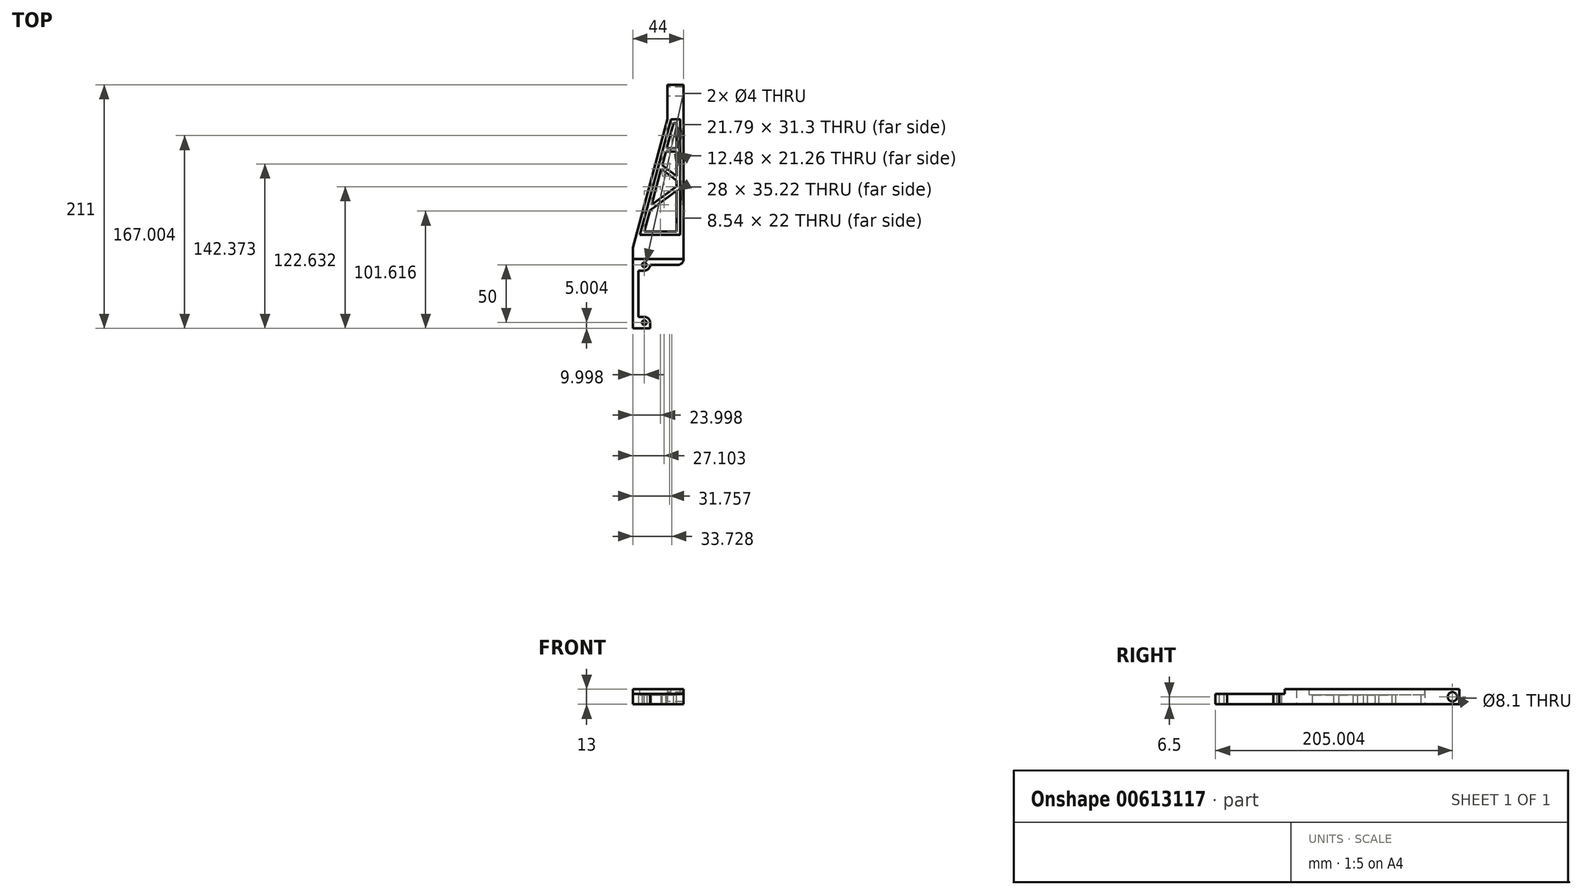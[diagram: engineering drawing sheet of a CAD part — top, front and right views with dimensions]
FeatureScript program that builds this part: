
annotation { "Feature Type Name" : "Feature", "Feature Type Description" : "" }
export const myFeature = defineFeature(function(context is Context, id is Id, definition is map)
    precondition{}
    {
        {
            var Q0;
            Q0=qCreatedBy(makeId("Top.planeOp"),FACE);
            var sketch = newSketch(context, id + "F0", { "sketchPlane" : qUnion([Q0])});
            skLineSegment(sketch, "E0.MirrorCS", {"start": v(-7.56, -43.6) * mm, "end": v(-7.56, -38.6) * mm});
            skCircle(sketch, "E1.MirrorC", {"center": v(-12.56, -38.6) * mm, "radius": 2 * mm});
            skCircle(sketch, "E2.MirrorC", {"center": v(-12.56, -88.6) * mm, "radius": 2 * mm});
            skLineSegment(sketch, "E3.MirrorCS", {"start": v(-7.56, -83.6) * mm, "end": v(-17.56, -83.6) * mm});
            skPoint(sketch, "E4.MirrorP", {"position": v(21.44, 117.4) * mm});
            skLineSegment(sketch, "E5.MirrorCS", {"start": v(7.44, 117.4) * mm, "end": v(7.44, 87.4) * mm});
            skLineSegment(sketch, "E6.MirrorCS", {"start": v(7.44, 87.4) * mm, "end": v(-22.56, -23.6) * mm});
            skPoint(sketch, "E7.MirrorP", {"position": v(-12.56, -83.6) * mm});
            skLineSegment(sketch, "E8.MirrorCS", {"start": v(-22.56, -23.6) * mm, "end": v(-22.56, -93.6) * mm});
            skLineSegment(sketch, "E9.MirrorCS", {"start": v(-22.56, -93.6) * mm, "end": v(-7.56, -93.6) * mm});
            skLineSegment(sketch, "E10.MirrorCS", {"start": v(-7.56, -93.6) * mm, "end": v(-7.56, -83.6) * mm});
            skLineSegment(sketch, "E11.MirrorCS", {"start": v(-17.56, -83.6) * mm, "end": v(-17.56, -43.6) * mm});
            skLineSegment(sketch, "E12.MirrorCS", {"start": v(-17.56, -43.6) * mm, "end": v(-7.56, -43.6) * mm});
            skLineSegment(sketch, "E13.MirrorCS", {"start": v(-7.56, -38.6) * mm, "end": v(21.44, -38.6) * mm});
            skLineSegment(sketch, "E14.MirrorCS", {"start": v(21.44, -38.6) * mm, "end": v(21.44, 117.4) * mm});
            skLineSegment(sketch, "E15.MirrorCS", {"start": v(-22.56, -33.6) * mm, "end": v(21.44, -33.6) * mm});
            skLineSegment(sketch, "E16.MirrorCS", {"start": v(21.44, 117.4) * mm, "end": v(7.44, 117.4) * mm});
            skSolve(sketch);
        }
        {
            var Q0;
            Q0=makeQuery(id+"F0.imprint","IMPRINT",FACE,{"disambiguationData":[TD([[makeQuery(id+"F0.imprint","IMPRINT",EDGE,{"derivedFrom":sQuery(id+"F0.wireOp",EDGE,"E5.MirrorCS")}),1.0]])]});
            extrude(context, id + "F1", {"entities" : qUnion([Q0]), "depth" : 13 * mm, "offsetDistance" : 25 * mm});
        }
        {
            var Q0;
            Q0=makeQuery(id+"F0.imprint","IMPRINT",FACE,{"disambiguationData":[TD([[makeQuery(id+"F0.imprint","IMPRINT",EDGE,{"derivedFrom":sQuery(id+"F0.wireOp",EDGE,"E0.MirrorCS")}),1.0]])]});
            extrude(context, id + "F2", {"entities" : qUnion([Q0]), "operationType" : NewBodyOperationType.ADD, "depth" : 9 * mm, "offsetDistance" : 25 * mm});
        }
        {
            var Q0;
            Q0=makeQuery(id+"F1.opExtrude","CAP_FACE",FACE,{"disambiguationData":[OSD([sQuery(id+"F0.wireOp",EDGE,"E5.MirrorCS"),sQuery(id+"F0.wireOp",EDGE,"E6.MirrorCS"),sQuery(id+"F0.wireOp",EDGE,"E8.MirrorCS"),sQuery(id+"F0.wireOp",EDGE,"E14.MirrorCS"),sQuery(id+"F0.wireOp",EDGE,"E15.MirrorCS"),sQuery(id+"F0.wireOp",EDGE,"E16.MirrorCS")])],"isStart":false});
            var sketch = newSketch(context, id + "F3", { "sketchPlane" : qUnion([Q0])});
            skLineSegment(sketch, "E17", {"start": v(18.44, -12.6) * mm, "end": v(-16.48, -12.6) * mm});
            skLineSegment(sketch, "E18", {"start": v(-16.48, -12.6) * mm, "end": v(10.55, 87.4) * mm});
            skLineSegment(sketch, "E19", {"start": v(18.44, 87.4) * mm, "end": v(18.44, -12.6) * mm});
            skLineSegment(sketch, "E20", {"start": v(18.44, 87.4) * mm, "end": v(10.55, 87.4) * mm});
            skSolve(sketch);
        }
        {
            var Q0;
            Q0=makeQuery(id+"F3.imprint","IMPRINT",FACE,{"disambiguationData":[TD([[makeQuery(id+"F3.imprint","IMPRINT",EDGE,{"derivedFrom":sQuery(id+"F3.wireOp",EDGE,"E17")}),-1.0]])]});
            extrude(context, id + "F4", {"entities" : qUnion([Q0]), "operationType" : NewBodyOperationType.REMOVE, "oppositeDirection" : true, "depth" : 5 * mm, "offsetDistance" : 25 * mm});
        }
        {
            var Q0;
            Q0=makeQuery(id+"F4.boolean.opBoolean","COPY",FACE,{"derivedFrom":makeQuery(id+"F4.opExtrude","CAP_FACE",FACE,{"disambiguationData":[OSD([sQuery(id+"F3.wireOp",EDGE,"E17"),sQuery(id+"F3.wireOp",EDGE,"E18"),sQuery(id+"F3.wireOp",EDGE,"E19"),sQuery(id+"F3.wireOp",EDGE,"E20")])],"isStart":false})});
            var sketch = newSketch(context, id + "F5", { "sketchPlane" : qUnion([Q0])});
            skLineSegment(sketch, "E21", {"start": v(15.44, 84.4) * mm, "end": v(15.44, -9.6) * mm});
            skLineSegment(sketch, "E22", {"start": v(15.44, -9.6) * mm, "end": v(-12.56, -9.6) * mm});
            skLineSegment(sketch, "E23", {"start": v(-12.56, -9.6) * mm, "end": v(12.84, 84.4) * mm});
            skLineSegment(sketch, "E24", {"start": v(12.84, 84.4) * mm, "end": v(15.44, 84.4) * mm});
            skLineSegment(sketch, "E25", {"start": v(15.44, 62.4) * mm, "end": v(6.9, 62.4) * mm});
            skLineSegment(sketch, "E26", {"start": v(15.44, 59.4) * mm, "end": v(6.09, 59.4) * mm});
            skLineSegment(sketch, "E27", {"start": v(2.96, 47.8) * mm, "end": v(15.44, 38.13) * mm});
            skLineSegment(sketch, "E28", {"start": v(2.1, 44.67) * mm, "end": v(15.44, 34.34) * mm});
            skLineSegment(sketch, "E29", {"start": v(15.44, 29.34) * mm, "end": v(-6.35, 13.37) * mm});
            skLineSegment(sketch, "E30", {"start": v(15.44, 25.62) * mm, "end": v(-7.6, 8.74) * mm});
            skSolve(sketch);
        }
        {
            var Q0;
            {var subQ0=sQuery(id+"F5.wireOp",EDGE,"E24");Q0=makeQuery(id+"F5.imprint","IMPRINT",FACE,{"disambiguationData":[TD([[makeQuery(id+"F5.imprint","IMPRINT",EDGE,{"derivedFrom":subQ0}),-1.0]])]});}
            var Q1;
            {var subQ0=sQuery(id+"F5.wireOp",EDGE,"E26");Q1=makeQuery(id+"F5.imprint","IMPRINT",FACE,{"disambiguationData":[TD([[makeQuery(id+"F5.imprint","IMPRINT",EDGE,{"derivedFrom":subQ0}),1.0]])]});}
            var Q2;
            {var subQ0=sQuery(id+"F5.wireOp",EDGE,"E28");Q2=makeQuery(id+"F5.imprint","IMPRINT",FACE,{"disambiguationData":[TD([[makeQuery(id+"F5.imprint","IMPRINT",EDGE,{"derivedFrom":subQ0}),-1.0]])]});}
            var Q3;
            {var subQ0=sQuery(id+"F5.wireOp",EDGE,"E22");Q3=makeQuery(id+"F5.imprint","IMPRINT",FACE,{"disambiguationData":[TD([[makeQuery(id+"F5.imprint","IMPRINT",EDGE,{"derivedFrom":subQ0}),-1.0]])]});}
            extrude(context, id + "F6", {"entities" : qUnion([Q0, Q1, Q2, Q3]), "operationType" : NewBodyOperationType.REMOVE, "endBound" : BoundingType.THROUGH_ALL, "oppositeDirection" : true, "depth" : 25 * mm, "offsetDistance" : 25 * mm});
        }
        {
            var Q0;
            Q0=makeQuery(id+"F2.opExtrude","SWEPT_EDGE",EDGE,{"disambiguationData":[OSD([sQuery(id+"F0.wireOp",EDGE,"E13.MirrorCS"),sQuery(id+"F0.wireOp",EDGE,"E14.MirrorCS")])]});
            fillet(context, id + "F7", {"entities" : qUnion([Q0]), "radius" : 5 * mm, "tangentPropagation" : true, "allowEdgeOverflow" : false});
        }
        {
            var Q0;
            Q0=makeQuery(id+"F2.opExtrude","SWEPT_EDGE",EDGE,{"disambiguationData":[OSD([sQuery(id+"F0.wireOp",EDGE,"E0.MirrorCS"),sQuery(id+"F0.wireOp",EDGE,"E12.MirrorCS")])]});
            fillet(context, id + "F8", {"entities" : qUnion([Q0]), "radius" : 5 * mm, "tangentPropagation" : true, "allowEdgeOverflow" : false});
        }
        {
            var Q0;
            Q0=makeQuery(id+"F2.opExtrude","SWEPT_EDGE",EDGE,{"disambiguationData":[OSD([sQuery(id+"F0.wireOp",EDGE,"E3.MirrorCS"),sQuery(id+"F0.wireOp",EDGE,"E10.MirrorCS")])]});
            fillet(context, id + "F9", {"entities" : qUnion([Q0]), "radius" : 5 * mm, "tangentPropagation" : true, "allowEdgeOverflow" : false});
        }
        {
            var Q0;
            Q0=makeQuery(id+"F1.opExtrude","SWEPT_FACE",FACE,{"disambiguationData":[OSD([sQuery(id+"F0.wireOp",EDGE,"E5.MirrorCS")])]});
            var sketch = newSketch(context, id + "F10", { "sketchPlane" : qUnion([Q0])});
            skCircle(sketch, "E31", {"center": v(-111.4, 6.5) * mm, "radius": 4.05 * mm});
            skSolve(sketch);
        }
        {
            var Q0;
            Q0=makeQuery(id+"F10.imprint","IMPRINT",FACE,{"disambiguationData":[TD([[makeQuery(id+"F10.imprint","IMPRINT",EDGE,{"derivedFrom":sQuery(id+"F10.wireOp",EDGE,"E31")}),1.0]])]});
            extrude(context, id + "F11", {"entities" : qUnion([Q0]), "operationType" : NewBodyOperationType.REMOVE, "endBound" : BoundingType.THROUGH_ALL, "oppositeDirection" : true, "depth" : 25 * mm, "offsetDistance" : 25 * mm});
        }
    });
